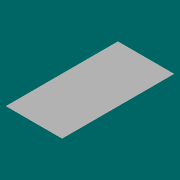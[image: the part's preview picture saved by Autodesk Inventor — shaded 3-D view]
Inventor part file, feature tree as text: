
AUTODESK INVENTOR PART (.ipt)
format: ipt  version: 2017 (Build 210142000, 142)  size: 74,752 bytes
history: native  units: in
note: dims shown in document units (in); Inventor stores cm internally (conversion verified against a paired STEP export)
features: extrude x1, sketch x1
ambient origin geometry x8: Origin, YZ Plane, XZ Plane, XY Plane, X Axis, Y Axis, Z Axis, Center Point
bodies: Solid1 (feature_tree)
feature tree (2):
  extrude  "Extrusion1"  Depth=96.0in
  sketch  "Sketch1"  dims[d0=48.0in d1=96.0in d2=0.1196in d3=0.0in]
